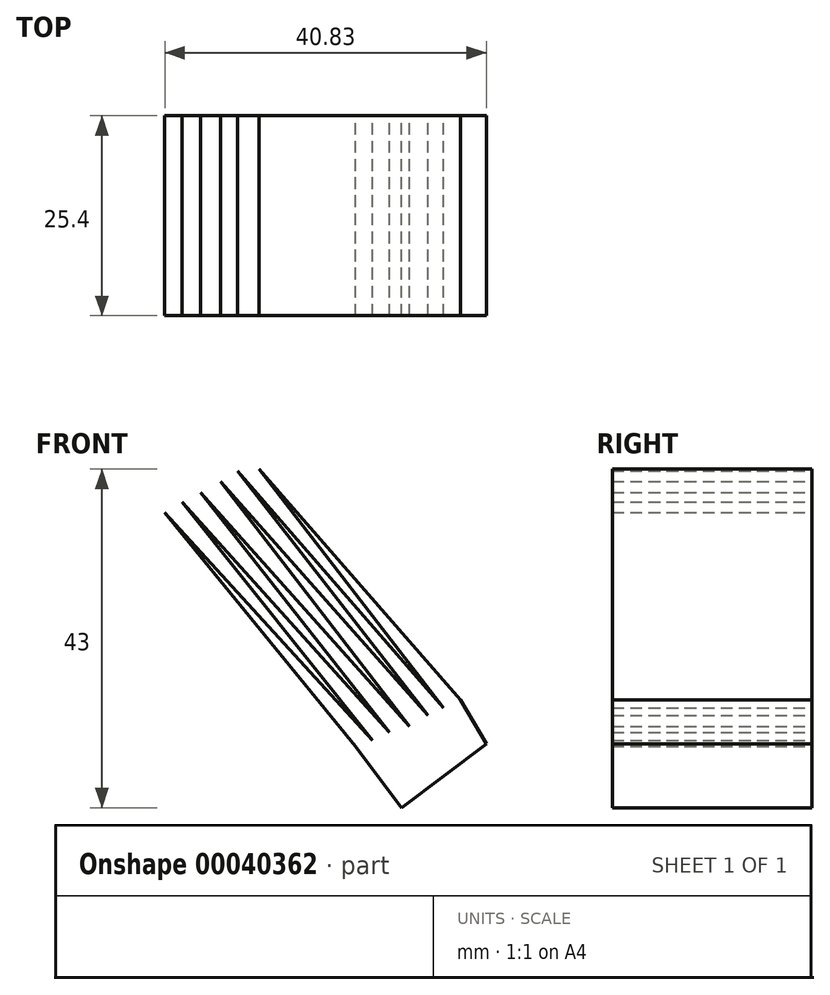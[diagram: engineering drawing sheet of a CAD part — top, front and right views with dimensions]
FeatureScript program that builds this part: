
annotation { "Feature Type Name" : "Feature", "Feature Type Description" : "" }
export const myFeature = defineFeature(function(context is Context, id is Id, definition is map)
    precondition{}
    {
        {
            var Q0;
            Q0=qCreatedBy(makeId("Front.planeOp"),FACE);
            var sketch = newSketch(context, id + "F0", { "sketchPlane" : qUnion([Q0])});
            skLineSegment(sketch, "E0", {"start": v(-61.21, 49.5) * mm, "end": v(-35.04, 20.96) * mm});
            skLineSegment(sketch, "E1", {"start": v(-35.04, 20.96) * mm, "end": v(-59.24, 50.68) * mm});
            skLineSegment(sketch, "E2", {"start": v(-59.24, 50.68) * mm, "end": v(-32.87, 21.75) * mm});
            skLineSegment(sketch, "E3", {"start": v(-32.87, 21.75) * mm, "end": v(-57.08, 52.06) * mm});
            skLineSegment(sketch, "E4", {"start": v(-57.08, 52.06) * mm, "end": v(-30.7, 22.73) * mm});
            skLineSegment(sketch, "E5", {"start": v(-30.7, 22.73) * mm, "end": v(-54.72, 53.24) * mm});
            skLineSegment(sketch, "E6", {"start": v(-54.72, 53.24) * mm, "end": v(-28.15, 23.52) * mm});
            skLineSegment(sketch, "E7", {"start": v(-28.15, 23.52) * mm, "end": v(-52.16, 54.62) * mm});
            skLineSegment(sketch, "E8", {"start": v(-52.16, 54.62) * mm, "end": v(-25.78, 24.9) * mm});
            skLineSegment(sketch, "E9", {"start": v(-25.78, 24.9) * mm, "end": v(-50, 56) * mm});
            skLineSegment(sketch, "E10", {"start": v(-50, 56) * mm, "end": v(-23.82, 25.88) * mm});
            skLineSegment(sketch, "E11", {"start": v(-23.82, 25.88) * mm, "end": v(-47.24, 56.2) * mm});
            skLineSegment(sketch, "E12", {"start": v(-47.24, 56.2) * mm, "end": v(-21.65, 26.87) * mm});
            skLineSegment(sketch, "E13", {"start": v(-21.65, 26.87) * mm, "end": v(-44.74, 57.6) * mm});
            skLineSegment(sketch, "E14", {"start": v(-61.21, 49.5) * mm, "end": v(-61.21, 67.17) * mm});
            skLineSegment(sketch, "E15", {"start": v(-61.21, 67.17) * mm, "end": v(-44.74, 57.6) * mm});
            skLineSegment(sketch, "E16", {"start": v(-35.04, 20.96) * mm, "end": v(-29.2, 13.2) * mm});
            skLineSegment(sketch, "E17", {"start": v(-29.2, 13.2) * mm, "end": v(-18.4, 21.3) * mm});
            skLineSegment(sketch, "E18", {"start": v(-18.4, 21.3) * mm, "end": v(-21.65, 26.87) * mm});
            skLineSegment(sketch, "E19", {"start": v(-44.74, 57.6) * mm, "end": v(-34.6, 65.21) * mm});
            skLineSegment(sketch, "E20", {"start": v(-34.6, 65.21) * mm, "end": v(-21.83, 43.35) * mm});
            skLineSegment(sketch, "E21", {"start": v(-21.83, 43.35) * mm, "end": v(-2.72, 38.22) * mm});
            skLineSegment(sketch, "E22", {"start": v(-2.72, 38.22) * mm, "end": v(-18.4, 21.3) * mm});
            skLineSegment(sketch, "E23", {"start": v(26.89, 98.24) * mm, "end": v(46.92, 119.85) * mm});
            skSolve(sketch);
        }
        {
            var Q0;
            Q0=makeQuery(id+"F0.imprint","IMPRINT",FACE,{"disambiguationData":[TD([[makeQuery(id+"F0.imprint","IMPRINT",EDGE,{"derivedFrom":sQuery(id+"F0.wireOp",EDGE,"E1")}),-1.0]])]});
            extrude(context, id + "F1", {"entities" : qUnion([Q0]), "depth" : 25.4 * mm});
        }
        {
            var Q0;
            Q0=makeQuery(id+"F0.imprint","IMPRINT",FACE,{"disambiguationData":[TD([[makeQuery(id+"F0.imprint","IMPRINT",EDGE,{"derivedFrom":sQuery(id+"F0.wireOp",EDGE,"E1")}),-1.0]])]});
            extrude(context, id + "F2", {"entities" : qUnion([Q0]), "operationType" : NewBodyOperationType.ADD, "depth" : 25.4 * mm});
        }
    });
